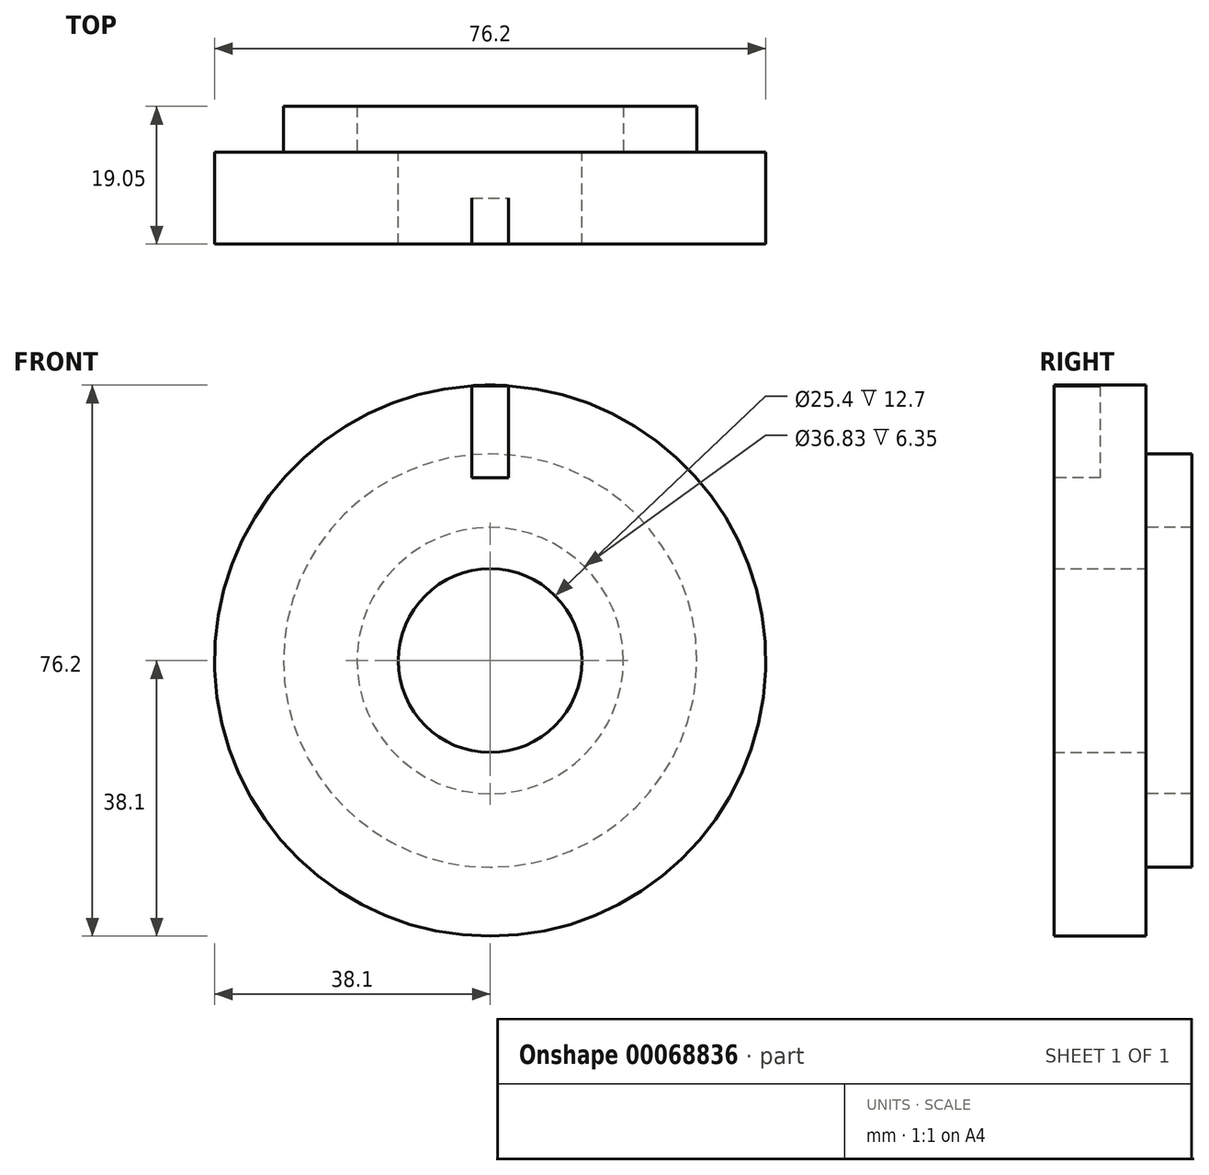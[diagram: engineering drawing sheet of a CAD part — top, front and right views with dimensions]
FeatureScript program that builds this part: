
annotation { "Feature Type Name" : "Feature", "Feature Type Description" : "" }
export const myFeature = defineFeature(function(context is Context, id is Id, definition is map)
    precondition{}
    {
        {
            var Q0;
            Q0=qCreatedBy(makeId("Front.planeOp"),FACE);
            var sketch = newSketch(context, id + "F0", { "sketchPlane" : qUnion([Q0])});
            skCircle(sketch, "E0", {"center": v(0, 0) * mm, "radius": 38.1 * mm});
            skCircle(sketch, "E1", {"center": v(0, 0) * mm, "radius": 12.7 * mm});
            skCircle(sketch, "E2", {"center": v(0, 0) * mm, "radius": 34.93 * mm, "construction": true});
            skPoint(sketch, "E3", {"position": v(0, 34.93) * mm});
            skPoint(sketch, "E4", {"position": v(-34.93, 0) * mm});
            skPoint(sketch, "E5", {"position": v(0, -34.92) * mm});
            skPoint(sketch, "E6", {"position": v(34.93, 0) * mm});
            skSolve(sketch);
        }
        {
            var Q0;
            Q0=qSketchRegion(id+"F0",true);
            extrude(context, id + "F1", {"entities" : qUnion([Q0]), "depth" : 12.7 * mm});
        }
        {
            var Q0;
            Q0=makeQuery(id+"F1.opExtrude","CAP_FACE",FACE,{"disambiguationData":[OSD([sQuery(id+"F0.wireOp",EDGE,"E0"),sQuery(id+"F0.wireOp",EDGE,"E1")])],"isStart":true});
            var sketch = newSketch(context, id + "F2", { "sketchPlane" : qUnion([Q0])});
            skCircle(sketch, "E7", {"center": v(0, 0) * mm, "radius": 18.41 * mm});
            skCircle(sketch, "E8", {"center": v(0, 0) * mm, "radius": 28.58 * mm});
            skSolve(sketch);
        }
        {
            var Q0;
            Q0=makeQuery(id+"F2.imprint","IMPRINT",FACE,{"disambiguationData":[TD([[makeQuery(id+"F2.imprint","IMPRINT",EDGE,{"derivedFrom":sQuery(id+"F2.wireOp",EDGE,"E7")}),-1.0]])]});
            extrude(context, id + "F3", {"entities" : qUnion([Q0]), "operationType" : NewBodyOperationType.ADD, "depth" : 6.35 * mm});
        }
        {
            var Q0;
            Q0=makeQuery(id+"F1.opExtrude","CAP_FACE",FACE,{"disambiguationData":[OSD([sQuery(id+"F0.wireOp",EDGE,"E0"),sQuery(id+"F0.wireOp",EDGE,"E1")])],"isStart":false});
            var sketch = newSketch(context, id + "F4", { "sketchPlane" : qUnion([Q0])});
            skLineSegment(sketch, "E9.bottom", {"start": v(-2.54, 38.02) * mm, "end": v(2.54, 38.02) * mm});
            skLineSegment(sketch, "E9.top", {"start": v(-2.54, 25.32) * mm, "end": v(2.54, 25.32) * mm});
            skLineSegment(sketch, "E9.left", {"start": v(-2.54, 38.02) * mm, "end": v(-2.54, 25.32) * mm});
            skLineSegment(sketch, "E9.right", {"start": v(2.54, 38.02) * mm, "end": v(2.54, 25.32) * mm});
            skSolve(sketch);
        }
        {
            var Q0;
            Q0 = qSketchRegion(id + "F4", true);
            extrude(context, id + "F5", {"entities" : qUnion([Q0]), "operationType" : NewBodyOperationType.REMOVE, "oppositeDirection" : true, "depth" : 6.35 * mm});
        }
    });
